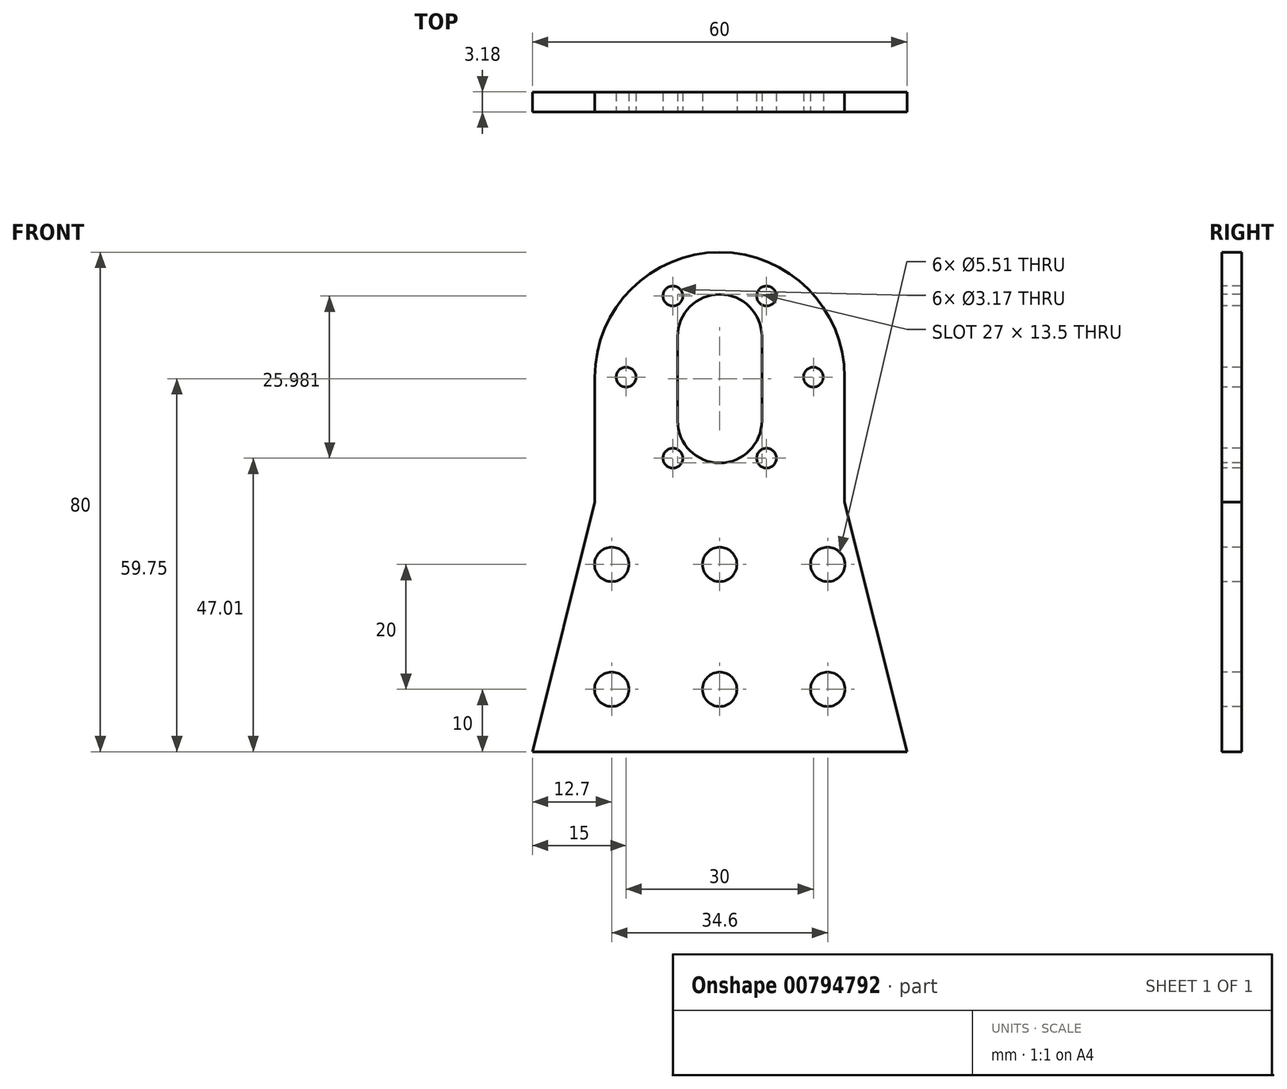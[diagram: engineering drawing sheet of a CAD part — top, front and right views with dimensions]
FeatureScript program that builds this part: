
annotation { "Feature Type Name" : "Feature", "Feature Type Description" : "" }
export const myFeature = defineFeature(function(context is Context, id is Id, definition is map)
    precondition{}
    {
        {
            var Q0;
            Q0=qCreatedBy(makeId("Front.planeOp"),FACE);
            var sketch = newSketch(context, id + "F0", { "sketchPlane" : qUnion([Q0])});
            skArc(sketch, "E0", {"start": v(20, 0) * mm, "mid": v(0, 20) * mm, "end": v(-20, 0) * mm});
            skPoint(sketch, "E1", {"position": v(20, 0) * mm});
            skPoint(sketch, "E2", {"position": v(-20, 0) * mm});
            skLineSegment(sketch, "E3", {"start": v(-20, 0) * mm, "end": v(-20, -20) * mm});
            skLineSegment(sketch, "E4", {"start": v(20, 0) * mm, "end": v(20, -20) * mm});
            skPoint(sketch, "E5", {"position": v(30, -60) * mm});
            skPoint(sketch, "E6", {"position": v(-30, -60) * mm});
            skPoint(sketch, "E7", {"position": v(20, -20) * mm});
            skPoint(sketch, "E8", {"position": v(-20, -20) * mm});
            skLineSegment(sketch, "E9", {"start": v(20, -20) * mm, "end": v(30, -60) * mm});
            skLineSegment(sketch, "E10", {"start": v(-20, -20) * mm, "end": v(-30, -60) * mm});
            skLineSegment(sketch, "E11", {"start": v(-30, -60) * mm, "end": v(30, -60) * mm});
            skCircle(sketch, "E12", {"center": v(0, 0) * mm, "radius": 15 * mm});
            skPoint(sketch, "E13", {"position": v(15, 0) * mm});
            skPoint(sketch, "E14.1.0", {"position": v(7.5, 13) * mm});
            skPoint(sketch, "E14.2.0", {"position": v(-7.5, 13) * mm});
            skPoint(sketch, "E14.3.0", {"position": v(-15, 0) * mm});
            skPoint(sketch, "E14.4.0", {"position": v(-7.5, -13) * mm});
            skPoint(sketch, "E14.5.0", {"position": v(7.5, -13) * mm});
            skPoint(sketch, "E15", {"position": v(0, 6.5) * mm});
            skPoint(sketch, "E15.positionSnap0", {"position": v(0, 20) * mm});
            skArc(sketch, "E16", {"start": v(6.75, 6.5) * mm, "mid": v(0, 13.25) * mm, "end": v(-6.75, 6.5) * mm});
            skPoint(sketch, "E17", {"position": v(0, -7) * mm});
            skArc(sketch, "E18", {"start": v(-6.75, -7) * mm, "mid": v(0, -13.75) * mm, "end": v(6.75, -7) * mm});
            skPoint(sketch, "E19", {"position": v(-6.75, -7) * mm});
            skPoint(sketch, "E20", {"position": v(6.75, 6.5) * mm});
            skPoint(sketch, "E21", {"position": v(6.75, -7) * mm});
            skPoint(sketch, "E22", {"position": v(-6.75, 6.5) * mm});
            skLineSegment(sketch, "E23", {"start": v(6.75, 6.5) * mm, "end": v(6.75, -7) * mm});
            skLineSegment(sketch, "E24", {"start": v(-6.75, 6.5) * mm, "end": v(-6.75, -7) * mm});
            skPoint(sketch, "E25", {"position": v(0, -50) * mm});
            skPoint(sketch, "E25.positionSnap0", {"position": v(0, -60) * mm});
            skPoint(sketch, "E26", {"position": v(0, -30) * mm});
            skPoint(sketch, "E27", {"position": v(-17.3, -60) * mm});
            skPoint(sketch, "E28", {"position": v(-17.3, -50) * mm});
            skPoint(sketch, "E29", {"position": v(-17.3, -30) * mm});
            skPoint(sketch, "E30", {"position": v(17.3, -60) * mm});
            skPoint(sketch, "E31", {"position": v(17.3, -50) * mm});
            skPoint(sketch, "E32", {"position": v(17.3, -30) * mm});
            skCircle(sketch, "E33", {"center": v(-17.3, -30) * mm, "radius": 2.76 * mm});
            skCircle(sketch, "E34", {"center": v(0, -30) * mm, "radius": 2.76 * mm});
            skCircle(sketch, "E35", {"center": v(17.3, -30) * mm, "radius": 2.76 * mm});
            skCircle(sketch, "E36", {"center": v(-17.3, -50) * mm, "radius": 2.76 * mm});
            skCircle(sketch, "E37", {"center": v(0, -50) * mm, "radius": 2.76 * mm});
            skCircle(sketch, "E38", {"center": v(17.3, -50) * mm, "radius": 2.76 * mm});
            skCircle(sketch, "E39", {"center": v(-7.5, 13) * mm, "radius": 1.59 * mm});
            skCircle(sketch, "E40", {"center": v(7.5, 13) * mm, "radius": 1.59 * mm});
            skCircle(sketch, "E41", {"center": v(15, 0) * mm, "radius": 1.59 * mm});
            skCircle(sketch, "E42", {"center": v(7.5, -13) * mm, "radius": 1.59 * mm});
            skCircle(sketch, "E43", {"center": v(-7.5, -13) * mm, "radius": 1.59 * mm});
            skCircle(sketch, "E44", {"center": v(-15, 0) * mm, "radius": 1.59 * mm});
            skSolve(sketch);
        }
        {
            var Q0;
            Q0=makeQuery(id+"F0.imprint","IMPRINT",FACE,{"disambiguationData":[TD([[makeQuery(id+"F0.imprint","IMPRINT",EDGE,{"derivedFrom":sQuery(id+"F0.wireOp",EDGE,"E0")}),1.0]])]});
            var Q1;
            Q1=makeQuery(id+"F0.imprint","IMPRINT",FACE,{"disambiguationData":[TD([[makeQuery(id+"F0.imprint","IMPRINT",EDGE,{"derivedFrom":sQuery(id+"F0.wireOp",EDGE,"E12")}),1.0]])]});
            extrude(context, id + "F1", {"entities" : qUnion([Q0, Q1]), "oppositeDirection" : true, "depth" : 3.17 * mm, "offsetDistance" : 25.4 * mm});
        }
    });
